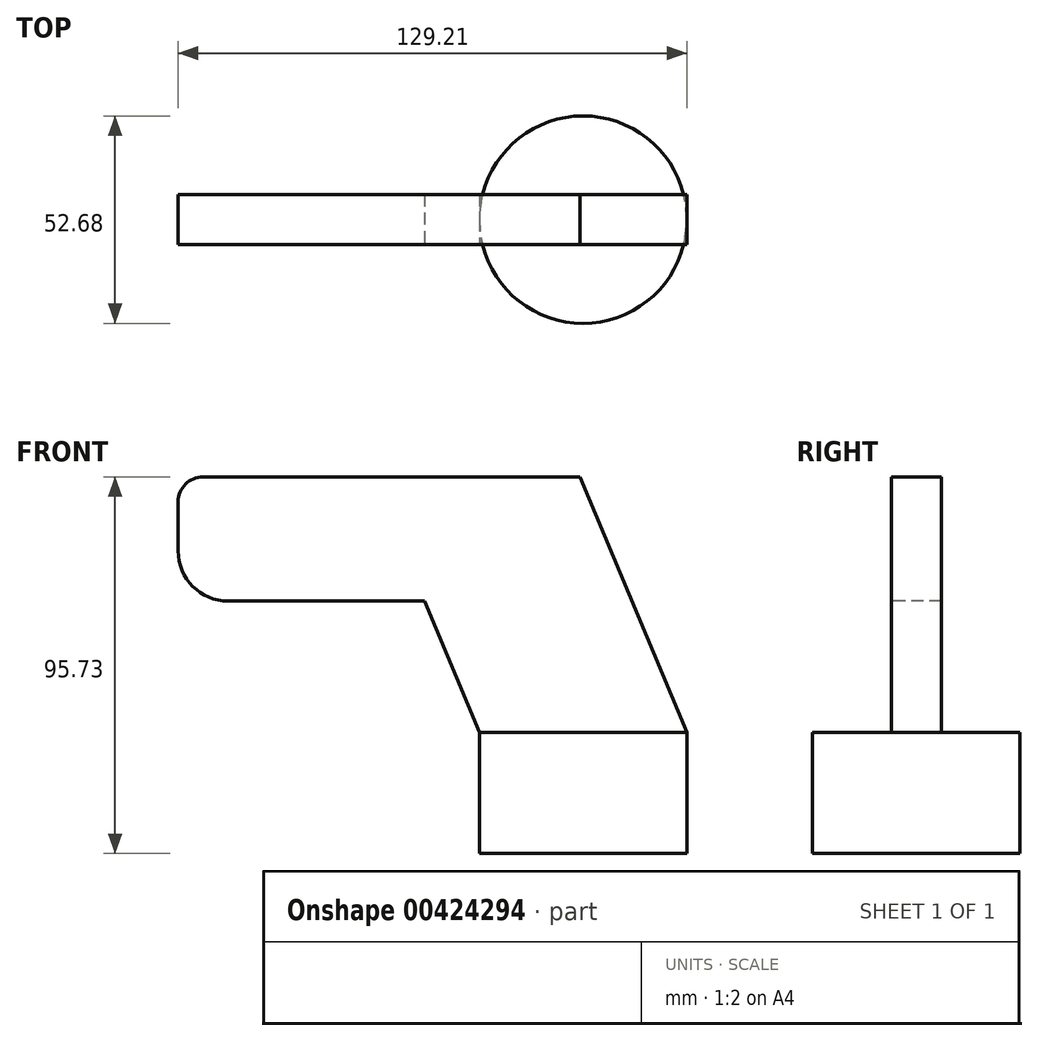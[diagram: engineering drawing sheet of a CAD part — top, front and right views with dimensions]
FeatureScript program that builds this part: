
annotation { "Feature Type Name" : "Feature", "Feature Type Description" : "" }
export const myFeature = defineFeature(function(context is Context, id is Id, definition is map)
    precondition{}
    {
        {
            var Q0;
            Q0=qCreatedBy(makeId("Front.planeOp"),FACE);
            var sketch = newSketch(context, id + "F0", { "sketchPlane" : qUnion([Q0])});
            skLineSegment(sketch, "E0", {"start": v(28.43, 0) * mm, "end": v(1.33, 65) * mm});
            skLineSegment(sketch, "E1", {"start": v(-100.78, 58.65) * mm, "end": v(-100.78, 46.12) * mm});
            skLineSegment(sketch, "E2", {"start": v(-88.08, 33.42) * mm, "end": v(-38.19, 33.42) * mm});
            skLineSegment(sketch, "E3", {"start": v(-38.19, 33.42) * mm, "end": v(-24.25, 0) * mm});
            skLineSegment(sketch, "E4", {"start": v(-24.25, 0) * mm, "end": v(28.43, 0) * mm});
            skLineSegment(sketch, "E5", {"start": v(-94.43, 65) * mm, "end": v(1.33, 65) * mm});
            skPoint(sketch, "E6.visualSharp", {"position": v(-100.78, 65) * mm});
            skArc(sketch, "E6.filletArc", {"start": v(-94.43, 65) * mm, "mid": v(-98.92, 63.14) * mm, "end": v(-100.78, 58.65) * mm});
            skPoint(sketch, "E7.visualSharp", {"position": v(-100.78, 33.42) * mm});
            skArc(sketch, "E7.filletArc", {"start": v(-100.78, 46.12) * mm, "mid": v(-97.06, 37.14) * mm, "end": v(-88.08, 33.42) * mm});
            skSolve(sketch);
        }
        {
            var Q0;
            Q0=makeQuery(id+"F0.imprint","IMPRINT",FACE,{"disambiguationData":[TD([[makeQuery(id+"F0.imprint","IMPRINT",EDGE,{"derivedFrom":sQuery(id+"F0.wireOp",EDGE,"E0")}),1.0]])]});
            extrude(context, id + "F1", {"entities" : qUnion([Q0]), "endBound" : BoundingType.SYMMETRIC, "oppositeDirection" : true, "depth" : 12.7 * mm});
        }
        {
            var Q0;
            Q0=qCreatedBy(makeId("Top.planeOp"),FACE);
            var sketch = newSketch(context, id + "F2", { "sketchPlane" : qUnion([Q0])});
            skCircle(sketch, "E8", {"center": v(2.1, 0) * mm, "radius": 26.34 * mm});
            skSolve(sketch);
        }
        {
            var Q0;
            Q0 = qSketchRegion(id + "F2", true);
            extrude(context, id + "F3", {"entities" : qUnion([Q0]), "operationType" : NewBodyOperationType.ADD, "oppositeDirection" : true, "depth" : 30.73 * mm});
        }
    });
